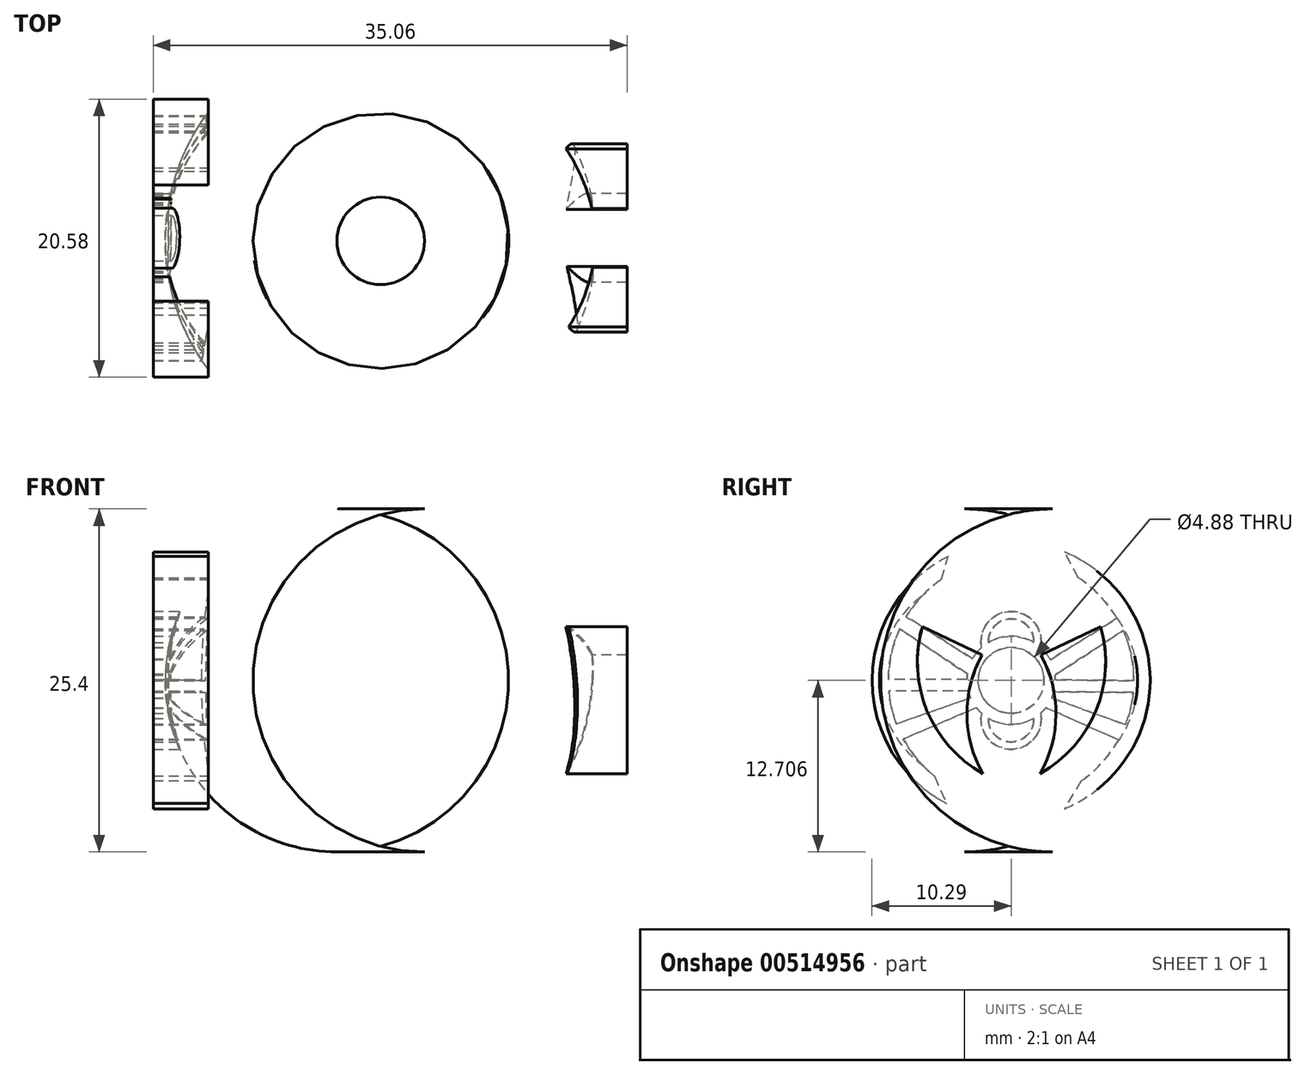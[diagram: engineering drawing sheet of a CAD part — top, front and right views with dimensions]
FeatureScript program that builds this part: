
annotation { "Feature Type Name" : "Feature", "Feature Type Description" : "" }
export const myFeature = defineFeature(function(context is Context, id is Id, definition is map)
    precondition{}
    {
        {
            var Q0;
            Q0=qCreatedBy(makeId("Top.planeOp"),FACE);
            var sketch = newSketch(context, id + "F0", { "sketchPlane" : qUnion([Q0])});
            skCircle(sketch, "E0", {"center": v(-41.33, 20.83) * mm, "radius": 15.94 * mm});
            skSolve(sketch);
        }
        {
            var Q0;
            Q0=makeQuery(id+"F0.imprint","IMPRINT",FACE,{"disambiguationData":[TD([[makeQuery(id+"F0.imprint","IMPRINT",EDGE,{"derivedFrom":sQuery(id+"F0.wireOp",EDGE,"E0")}),1.0]])]});
            extrude(context, id + "F1", {"entities" : qUnion([Q0]), "depth" : 25.4 * mm, "offsetDistance" : 25.4 * mm});
        }
        {
            var Q0;
            Q0=makeQuery(id+"F1.opExtrude","CAP_EDGE",EDGE,{"disambiguationData":[OSD([sQuery(id+"F0.wireOp",EDGE,"E0")])],"isStart":false});
            var Q1;
            Q1=makeQuery(id+"F1.opExtrude","CAP_EDGE",EDGE,{"disambiguationData":[OSD([sQuery(id+"F0.wireOp",EDGE,"E0")])],"isStart":true});
            fillet(context, id + "F2", {"entities" : qUnion([Q0, Q1]), "radius" : 12.7 * mm, "tangentPropagation" : true, "allowEdgeOverflow" : false});
        }
        {
            var Q0;
            Q0=qCreatedBy(makeId("Front.planeOp"),FACE);
            cPlane(context, id + "F3", {"entities" : qUnion([Q0]), "cplaneType" : CPlaneType.OFFSET, "offset" : 8.64 * mm, "oppositeDirection" : true, "width" : 152.4 * mm, "height" : 152.4 * mm});
        }
        {
            var Q0;
            Q0=qCreatedBy(id+"F3.planeOp",FACE);
            var sketch = newSketch(context, id + "F4", { "sketchPlane" : qUnion([Q0])});
            skCircle(sketch, "E1", {"center": v(-41.45, 12.33) * mm, "radius": 9.37 * mm});
            skSolve(sketch);
        }
        {
            var Q0;
            Q0 = qSketchRegion(id + "F4", true);
            extrude(context, id + "F5", {"entities" : qUnion([Q0]), "operationType" : NewBodyOperationType.ADD, "depth" : 3.8 * mm, "offsetDistance" : 25.4 * mm});
        }
        {
            var Q0;
            Q0=makeQuery(id+"F5.opExtrude","CAP_FACE",FACE,{"disambiguationData":[OSD([sQuery(id+"F4.wireOp",EDGE,"E1")])],"isStart":false});
            var sketch = newSketch(context, id + "F6", { "sketchPlane" : qUnion([Q0])});
            skArc(sketch, "E2", {"start": v(-44.1, 12.14) * mm, "mid": v(-42.36, 15.52) * mm, "end": v(-43.95, 18.97) * mm});
            skArc(sketch, "E3", {"start": v(-38.5, 12.1) * mm, "mid": v(-39.38, 16.99) * mm, "end": v(-43.95, 18.97) * mm});
            skArc(sketch, "E4", {"start": v(-44.1, 12.14) * mm, "mid": v(-41.37, 4.61) * mm, "end": v(-38.5, 12.1) * mm});
            skFitSpline(sketch, "E5", {"points": [v(-38.5, 12.1) * mm, v(-39.48, 12.1) * mm, v(-40.78, 11.82) * mm, v(-42.02, 11.08) * mm, v(-42.74, 9.9) * mm, v(-42.66, 8.59) * mm, v(-41.87, 7.72) * mm, v(-40.52, 7.67) * mm, v(-39.48, 8.36) * mm, v(-39.18, 9.27) * mm, v(-39.18, 9.83) * mm, v(-39.46, 9.86) * mm, v(-39.7, 9.1) * mm, v(-39.94, 8.56) * mm, v(-40.45, 8.2) * mm, v(-41.33, 8.13) * mm, v(-41.9, 8.33) * mm, v(-42.18, 8.88) * mm, v(-42.2, 9.65) * mm, v(-41.9, 10.5) * mm, v(-41.33, 10.82) * mm, v(-40.68, 11.2) * mm, v(-39.76, 11.46) * mm, v(-38.5, 11.61) * mm, v(-38.5, 12.1) * mm]});
            skLineSegment(sketch, "E6", {"start": v(-38.5, 11.62) * mm, "end": v(-39.76, 11.46) * mm});
            skPoint(sketch, "E7.end.orphan", {"position": v(-38.3, 11.62) * mm});
            skLineSegment(sketch, "E8", {"start": v(-40.67, 11.2) * mm, "end": v(-41.9, 10.5) * mm});
            skLineSegment(sketch, "E9", {"start": v(-38.5, 11.62) * mm, "end": v(-38.05, 11.62) * mm});
            skSolve(sketch);
        }
        {
            var Q0;
            {var subQ0=sQuery(id+"F6.wireOp",EDGE,"E2");Q0=makeQuery(id+"F6.imprint","IMPRINT",FACE,{"disambiguationData":[TD([[makeQuery(id+"F6.imprint","IMPRINT",EDGE,{"derivedFrom":subQ0}),-1.0]])]});}
            extrude(context, id + "F7", {"entities" : qUnion([Q0]), "operationType" : NewBodyOperationType.ADD, "depth" : 0.5 * mm, "offsetDistance" : 25.4 * mm});
        }
        {
            var Q0;
            Q0=makeQuery(id+"F7.opExtrude","CAP_FACE",FACE,{"disambiguationData":[OSD([sQuery(id+"F6.wireOp",EDGE,"E2"),sQuery(id+"F6.wireOp",EDGE,"E3"),sQuery(id+"F6.wireOp",EDGE,"E4")])],"isStart":false});
            var sketch = newSketch(context, id + "F8", { "sketchPlane" : qUnion([Q0])});
            skFitSpline(sketch, "E10", {"points": [v(-38.52, 12.04) * mm, v(-39.5, 12.04) * mm, v(-40.8, 11.76) * mm, v(-42.04, 11.02) * mm, v(-42.75, 9.85) * mm, v(-42.67, 8.53) * mm, v(-41.89, 7.67) * mm, v(-40.54, 7.62) * mm, v(-39.5, 8.3) * mm, v(-39.19, 9.22) * mm, v(-39.19, 9.78) * mm, v(-39.47, 9.8) * mm, v(-39.72, 9.04) * mm, v(-39.95, 8.5) * mm, v(-40.46, 8.15) * mm, v(-41.34, 8.07) * mm, v(-41.91, 8.28) * mm, v(-42.2, 8.83) * mm, v(-42.22, 9.6) * mm, v(-41.91, 10.44) * mm, v(-41.34, 10.77) * mm, v(-40.69, 11.15) * mm, v(-39.77, 11.4) * mm, v(-38.52, 11.56) * mm, v(-38.52, 12.04) * mm]});
            skLineSegment(sketch, "E11", {"start": v(-38.52, 11.56) * mm, "end": v(-39.77, 11.4) * mm});
            skLineSegment(sketch, "E12", {"start": v(-40.69, 11.15) * mm, "end": v(-41.91, 10.44) * mm});
            skLineSegment(sketch, "E13", {"start": v(-38.52, 11.56) * mm, "end": v(-38.06, 11.56) * mm});
            skLineSegment(sketch, "E14", {"start": v(-38.52, 12.04) * mm, "end": v(-38.06, 11.56) * mm});
            skLineSegment(sketch, "E15", {"start": v(-39.77, 11.4) * mm, "end": v(-39.78, 11.4) * mm});
            skSolve(sketch);
        }
        {
            var Q0;
            {var subQ1=sQuery(id+"F8.wireOp",EDGE,"E10");Q0=makeQuery(id+"F8.imprint","IMPRINT",FACE,{"disambiguationData":[TD([[makeQuery(id+"F8.imprint","IMPRINT",EDGE,{"derivedFrom":subQ1}),1.0]])]});}
            extrude(context, id + "F9", {"entities" : qUnion([Q0]), "operationType" : NewBodyOperationType.REMOVE, "oppositeDirection" : true, "depth" : 2.54 * mm, "offsetDistance" : 25.4 * mm});
        }
        {
            var Q0;
            Q0=qCreatedBy(makeId("Right.planeOp"),FACE);
            cPlane(context, id + "F10", {"entities" : qUnion([Q0]), "cplaneType" : CPlaneType.OFFSET, "offset" : 28.2 * mm, "oppositeDirection" : true, "width" : 152.4 * mm, "height" : 152.4 * mm});
        }
        {
            var Q0;
            Q0=qCreatedBy(id+"F10.planeOp",FACE);
            var sketch = newSketch(context, id + "F11", { "sketchPlane" : qUnion([Q0])});
            skLineSegment(sketch, "E16", {"start": v(14.46, 16.7) * mm, "end": v(18.88, 14.58) * mm});
            skLineSegment(sketch, "E17.MirrorCS", {"start": v(27.65, 16.7) * mm, "end": v(23.24, 14.58) * mm});
            skArc(sketch, "E18", {"start": v(14.46, 16.7) * mm, "mid": v(14.8, 10.47) * mm, "end": v(18.94, 5.8) * mm});
            skArc(sketch, "E19", {"start": v(18.88, 14.58) * mm, "mid": v(17.76, 10.18) * mm, "end": v(18.94, 5.8) * mm});
            skArc(sketch, "E20.MirrorCS", {"start": v(23.24, 14.58) * mm, "mid": v(24.35, 10.18) * mm, "end": v(23.17, 5.8) * mm});
            skArc(sketch, "E21.MirrorCS", {"start": v(27.65, 16.7) * mm, "mid": v(27.3, 10.47) * mm, "end": v(23.17, 5.8) * mm});
            skSolve(sketch);
        }
        {
            var Q0;
            Q0 = qSketchRegion(id + "F11", true);
            extrude(context, id + "F12", {"entities" : qUnion([Q0]), "operationType" : NewBodyOperationType.ADD, "depth" : 5.08 * mm, "offsetDistance" : 25.4 * mm});
        }
        {
            var Q0;
            Q0=qCreatedBy(makeId("Right.planeOp"),FACE);
            cPlane(context, id + "F13", {"entities" : qUnion([Q0]), "cplaneType" : CPlaneType.OFFSET, "offset" : 54.1 * mm, "oppositeDirection" : true, "width" : 152.4 * mm, "height" : 152.4 * mm});
        }
        {
            var Q0;
            Q0=qCreatedBy(id+"F13.planeOp",FACE);
            var sketch = newSketch(context, id + "F14", { "sketchPlane" : qUnion([Q0])});
            skArc(sketch, "E22", {"start": v(12.8, 16.52) * mm, "mid": v(12.17, 14.7) * mm, "end": v(11.95, 12.78) * mm});
            skArc(sketch, "E23", {"start": v(17.8, 13.18) * mm, "mid": v(17.77, 12.98) * mm, "end": v(17.76, 12.78) * mm});
            skCircle(sketch, "E24", {"center": v(21.03, 12.7) * mm, "radius": 2.44 * mm});
            skArc(sketch, "E25", {"start": v(18.85, 10.27) * mm, "mid": v(21.03, 7.6) * mm, "end": v(23.21, 10.27) * mm});
            skArc(sketch, "E26", {"start": v(19.35, 9.9) * mm, "mid": v(21.03, 8.15) * mm, "end": v(22.7, 9.9) * mm});
            skPoint(sketch, "E27.center.orphan", {"position": v(21.03, 15.53) * mm});
            skArc(sketch, "E28.MirrorC", {"start": v(18.85, 15.14) * mm, "mid": v(21.03, 17.8) * mm, "end": v(23.21, 15.14) * mm});
            skArc(sketch, "E29.MirrorC", {"start": v(19.35, 15.51) * mm, "mid": v(21.03, 17.26) * mm, "end": v(22.7, 15.51) * mm});
            skPoint(sketch, "E30.start.orphan", {"position": v(26.12, 12.7) * mm});
            skLineSegment(sketch, "E31", {"start": v(18.17, 14.3) * mm, "end": v(13.27, 17.42) * mm});
            skLineSegment(sketch, "E32", {"start": v(17.8, 13.18) * mm, "end": v(12.8, 16.52) * mm});
            skLineSegment(sketch, "E33", {"start": v(17.76, 12.78) * mm, "end": v(11.95, 12.78) * mm});
            skLineSegment(sketch, "E34", {"start": v(17.86, 11.9) * mm, "end": v(11.99, 11.9) * mm});
            skLineSegment(sketch, "E35", {"start": v(18.03, 11.42) * mm, "end": v(12.54, 9.48) * mm});
            skLineSegment(sketch, "E36", {"start": v(18.46, 10.69) * mm, "end": v(13.06, 8.37) * mm});
            skLineSegment(sketch, "E37.MirrorCS", {"start": v(23.98, 14.27) * mm, "end": v(28.92, 17.34) * mm});
            skLineSegment(sketch, "E38.MirrorCS", {"start": v(24.35, 13.14) * mm, "end": v(29.39, 16.43) * mm});
            skLineSegment(sketch, "E39.MirrorCS", {"start": v(24.38, 12.74) * mm, "end": v(30.19, 12.68) * mm});
            skLineSegment(sketch, "E40.MirrorCS", {"start": v(24.27, 11.87) * mm, "end": v(30.14, 11.8) * mm});
            skLineSegment(sketch, "E41.MirrorCS", {"start": v(24.1, 11.38) * mm, "end": v(29.56, 9.4) * mm});
            skLineSegment(sketch, "E42.MirrorCS", {"start": v(23.66, 10.66) * mm, "end": v(29.04, 8.28) * mm});
            skPoint(sketch, "E43.orphan", {"position": v(21.03, 5.04) * mm});
            skLineSegment(sketch, "E44", {"start": v(15.35, 5.63) * mm, "end": v(16.26, 3.6) * mm});
            skLineSegment(sketch, "E45", {"start": v(26.23, 5.27) * mm, "end": v(24.97, 3.2) * mm});
            skLineSegment(sketch, "E46", {"start": v(15.87, 20.18) * mm, "end": v(16.37, 21.88) * mm});
            skLineSegment(sketch, "E47", {"start": v(25.99, 20.3) * mm, "end": v(24.99, 22.2) * mm});
            skArc(sketch, "E48", {"start": v(25, 22.2) * mm, "mid": v(25, 22.2) * mm, "end": v(24.99, 22.2) * mm});
            skArc(sketch, "E49", {"start": v(16.36, 21.87) * mm, "mid": v(10.74, 12.77) * mm, "end": v(16.26, 3.6) * mm});
            skArc(sketch, "E50", {"start": v(16.37, 21.88) * mm, "mid": v(16.37, 21.88) * mm, "end": v(16.36, 21.87) * mm});
            skArc(sketch, "E51.trimOffspring", {"start": v(11.99, 11.9) * mm, "mid": v(13.03, 8.42) * mm, "end": v(15.35, 5.63) * mm});
            skArc(sketch, "E52.trimOffspring", {"start": v(17.86, 11.9) * mm, "mid": v(17.93, 11.66) * mm, "end": v(18.03, 11.42) * mm});
            skArc(sketch, "E53.trimOffspring", {"start": v(18.46, 10.69) * mm, "mid": v(18.64, 10.47) * mm, "end": v(18.85, 10.27) * mm});
            skArc(sketch, "E54.trimOffspring", {"start": v(18.85, 15.14) * mm, "mid": v(18.48, 14.75) * mm, "end": v(18.17, 14.3) * mm});
            skArc(sketch, "E55.trimOffspring", {"start": v(22.7, 15.51) * mm, "mid": v(21.03, 15.98) * mm, "end": v(19.35, 15.51) * mm});
            skArc(sketch, "E56.trimOffspring", {"start": v(19.35, 9.9) * mm, "mid": v(21.03, 9.44) * mm, "end": v(22.7, 9.9) * mm});
            skArc(sketch, "E57.trimOffspring", {"start": v(23.21, 10.27) * mm, "mid": v(23.42, 10.47) * mm, "end": v(23.6, 10.7) * mm});
            skLineSegment(sketch, "E58", {"start": v(24.1, 11.38) * mm, "end": v(24.03, 11.41) * mm});
            skLineSegment(sketch, "E59", {"start": v(23.66, 10.66) * mm, "end": v(23.6, 10.7) * mm});
            skLineSegment(sketch, "E60", {"start": v(24.27, 11.87) * mm, "end": v(24.2, 11.87) * mm});
            skLineSegment(sketch, "E61", {"start": v(24.38, 12.74) * mm, "end": v(24.3, 12.74) * mm});
            skLineSegment(sketch, "E62", {"start": v(24.3, 12.74) * mm, "end": v(24.3, 12.74) * mm});
            skArc(sketch, "E63", {"start": v(24.3, 12.74) * mm, "mid": v(24.3, 12.92) * mm, "end": v(24.28, 13.09) * mm});
            skArc(sketch, "E64.trimOffspring", {"start": v(24.03, 11.41) * mm, "mid": v(24.12, 11.64) * mm, "end": v(24.2, 11.87) * mm});
            skArc(sketch, "E65.trimOffspring", {"start": v(28.86, 17.3) * mm, "mid": v(27.6, 18.97) * mm, "end": v(25.99, 20.3) * mm});
            skArc(sketch, "E66.trimOffspring", {"start": v(29.49, 9.42) * mm, "mid": v(29.86, 10.6) * mm, "end": v(30.06, 11.8) * mm});
            skArc(sketch, "E67.trimOffspring", {"start": v(30.1, 12.68) * mm, "mid": v(29.91, 14.58) * mm, "end": v(29.32, 16.4) * mm});
            skArc(sketch, "E68.trimOffspring", {"start": v(15.87, 20.18) * mm, "mid": v(14.43, 18.94) * mm, "end": v(13.27, 17.42) * mm});
            skArc(sketch, "E69.trimOffspring", {"start": v(26.23, 5.27) * mm, "mid": v(27.78, 6.63) * mm, "end": v(28.97, 8.31) * mm});
            skArc(sketch, "E70.trimOffspring", {"start": v(24.97, 3.2) * mm, "mid": v(31.32, 12.7) * mm, "end": v(25, 22.2) * mm});
            skLineSegment(sketch, "E71", {"start": v(23.98, 14.27) * mm, "end": v(23.93, 14.22) * mm});
            skLineSegment(sketch, "E72", {"start": v(24.35, 13.14) * mm, "end": v(24.28, 13.09) * mm});
            skArc(sketch, "E73.trimOffspring", {"start": v(23.93, 14.22) * mm, "mid": v(23.61, 14.71) * mm, "end": v(23.21, 15.14) * mm});
            skLineSegment(sketch, "E74", {"start": v(24.2, 11.87) * mm, "end": v(24.2, 11.87) * mm});
            skSolve(sketch);
        }
        {
            var Q0;
            Q0 = qSketchRegion(id + "F14", true);
            extrude(context, id + "F15", {"entities" : qUnion([Q0]), "operationType" : NewBodyOperationType.ADD, "depth" : -4.06 * mm, "offsetDistance" : 25.4 * mm});
        }
    });
